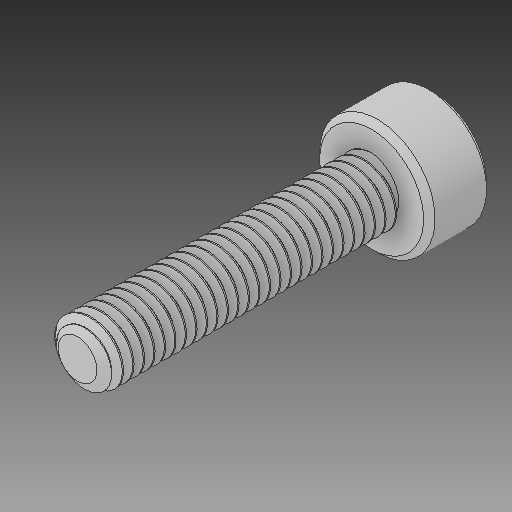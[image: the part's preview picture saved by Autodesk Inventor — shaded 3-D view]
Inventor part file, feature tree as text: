
AUTODESK INVENTOR PART (.ipt)
format: ipt  version: 2018 (Build 220112000, 112)  size: 925,696 bytes
history: native  units: in
note: dims shown in document units (in); Inventor stores cm internally (conversion verified against a paired STEP export)
features: chamfer x1
ambient origin geometry x8: Origin, YZ Plane, XZ Plane, XY Plane, X Axis, Y Axis, Z Axis, Center Point
bodies: Solid1 (feature_tree)
feature tree (1):
  chamfer  "Chamfer1"  [1 undecoded]
note: 1 required parameter value undecoded (feature->parameter linkage not recoverable at this tier; creation-order binding heuristic only, values carry confidence <= 0.55)
